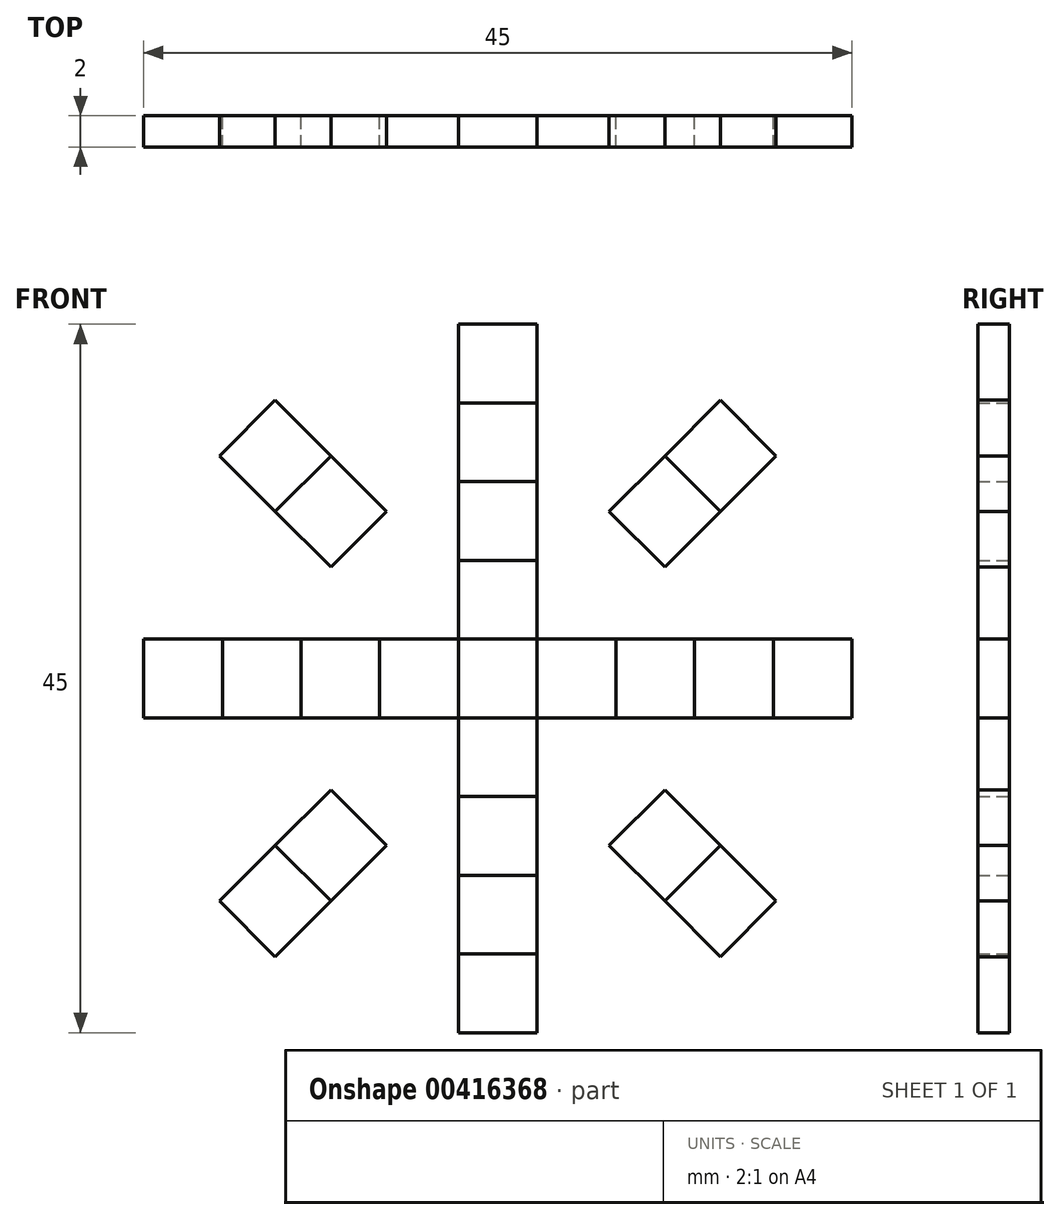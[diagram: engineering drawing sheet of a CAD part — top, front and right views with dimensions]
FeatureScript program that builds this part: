
annotation { "Feature Type Name" : "Feature", "Feature Type Description" : "" }
export const myFeature = defineFeature(function(context is Context, id is Id, definition is map)
    precondition{}
    {
        {
            var Q0;
            Q0=qCreatedBy(makeId("Front.planeOp"),FACE);
            var sketch = newSketch(context, id + "F0", { "sketchPlane" : qUnion([Q0])});
            skLineSegment(sketch, "E0", {"start": v(0, 0) * mm, "end": v(0, 2.5) * mm, "construction": true});
            skLineSegment(sketch, "E1", {"start": v(0, 2.5) * mm, "end": v(2.5, 2.5) * mm});
            skLineSegment(sketch, "E2", {"start": v(2.5, 2.5) * mm, "end": v(2.5, -2.5) * mm});
            skLineSegment(sketch, "E3", {"start": v(2.5, -2.5) * mm, "end": v(-2.5, -2.5) * mm});
            skLineSegment(sketch, "E4", {"start": v(-2.5, -2.5) * mm, "end": v(-2.5, 2.5) * mm});
            skLineSegment(sketch, "E5", {"start": v(-2.5, 2.5) * mm, "end": v(0, 2.5) * mm});
            skLineSegment(sketch, "E6", {"start": v(-2.5, 2.5) * mm, "end": v(-2.5, 7.5) * mm});
            skLineSegment(sketch, "E7", {"start": v(-2.5, 7.5) * mm, "end": v(2.5, 7.5) * mm});
            skLineSegment(sketch, "E8", {"start": v(2.5, 7.5) * mm, "end": v(2.5, 2.5) * mm});
            skLineSegment(sketch, "E9", {"start": v(2.5, 2.5) * mm, "end": v(7.5, 2.5) * mm});
            skLineSegment(sketch, "E10", {"start": v(7.5, 2.5) * mm, "end": v(7.5, -2.5) * mm});
            skLineSegment(sketch, "E11", {"start": v(7.5, -2.5) * mm, "end": v(2.5, -2.5) * mm});
            skLineSegment(sketch, "E12", {"start": v(2.5, -2.5) * mm, "end": v(2.5, -7.5) * mm});
            skLineSegment(sketch, "E13", {"start": v(2.5, -7.5) * mm, "end": v(-2.5, -7.5) * mm});
            skLineSegment(sketch, "E14", {"start": v(-2.5, -7.5) * mm, "end": v(-2.5, -2.5) * mm});
            skLineSegment(sketch, "E15", {"start": v(-2.5, -2.5) * mm, "end": v(-7.5, -2.5) * mm});
            skLineSegment(sketch, "E16", {"start": v(-7.5, -2.5) * mm, "end": v(-7.5, 2.5) * mm});
            skLineSegment(sketch, "E17", {"start": v(-7.5, 2.5) * mm, "end": v(-2.5, 2.5) * mm});
            skLineSegment(sketch, "E18", {"start": v(-7.5, -2.5) * mm, "end": v(-12.5, -2.5) * mm});
            skLineSegment(sketch, "E19", {"start": v(-12.5, -2.5) * mm, "end": v(-12.5, 2.5) * mm});
            skLineSegment(sketch, "E20", {"start": v(-12.5, 2.5) * mm, "end": v(-7.5, 2.5) * mm});
            skLineSegment(sketch, "E21", {"start": v(7.5, 2.5) * mm, "end": v(12.5, 2.5) * mm});
            skLineSegment(sketch, "E22", {"start": v(12.5, 2.5) * mm, "end": v(12.5, -2.5) * mm});
            skLineSegment(sketch, "E23", {"start": v(12.5, -2.5) * mm, "end": v(7.5, -2.5) * mm});
            skLineSegment(sketch, "E24", {"start": v(-2.5, 7.5) * mm, "end": v(-2.5, 12.5) * mm});
            skLineSegment(sketch, "E25", {"start": v(-2.5, 12.5) * mm, "end": v(2.5, 12.5) * mm});
            skLineSegment(sketch, "E26", {"start": v(2.5, 12.5) * mm, "end": v(2.5, 7.5) * mm});
            skLineSegment(sketch, "E27", {"start": v(2.5, -7.5) * mm, "end": v(2.5, -12.5) * mm});
            skLineSegment(sketch, "E28", {"start": v(2.5, -12.5) * mm, "end": v(-2.5, -12.5) * mm});
            skLineSegment(sketch, "E29", {"start": v(-2.5, -12.5) * mm, "end": v(-2.5, -7.5) * mm});
            skLineSegment(sketch, "E30", {"start": v(0, 2.5) * mm, "end": v(0, 12.5) * mm, "construction": true});
            skCircle(sketch, "E31.cCircle", {"center": v(0, 0) * mm, "radius": 12.5 * mm, "construction": true});
            skLineSegment(sketch, "E31.0", {"start": v(-5.18, 12.5) * mm, "end": v(5.18, 12.5) * mm, "construction": true});
            skLineSegment(sketch, "E31.1", {"start": v(5.18, 12.5) * mm, "end": v(12.5, 5.18) * mm, "construction": true});
            skLineSegment(sketch, "E31.2", {"start": v(12.5, 5.18) * mm, "end": v(12.5, -5.18) * mm, "construction": true});
            skLineSegment(sketch, "E31.3", {"start": v(12.5, -5.18) * mm, "end": v(5.18, -12.5) * mm, "construction": true});
            skLineSegment(sketch, "E31.4", {"start": v(5.18, -12.5) * mm, "end": v(-5.18, -12.5) * mm, "construction": true});
            skLineSegment(sketch, "E31.5", {"start": v(-5.18, -12.5) * mm, "end": v(-12.5, -5.18) * mm, "construction": true});
            skLineSegment(sketch, "E31.6", {"start": v(-12.5, -5.18) * mm, "end": v(-12.5, 5.18) * mm, "construction": true});
            skLineSegment(sketch, "E31.7", {"start": v(-12.5, 5.18) * mm, "end": v(-5.18, 12.5) * mm, "construction": true});
            skPoint(sketch, "E31.0.midPoint", {"position": v(0, 12.5) * mm});
            skLineSegment(sketch, "E32", {"start": v(8.84, 8.84) * mm, "end": v(10.6, 7.07) * mm});
            skLineSegment(sketch, "E33", {"start": v(10.6, 7.07) * mm, "end": v(14.14, 10.6) * mm});
            skLineSegment(sketch, "E34", {"start": v(14.14, 10.6) * mm, "end": v(10.6, 14.14) * mm});
            skLineSegment(sketch, "E35", {"start": v(8.84, 8.84) * mm, "end": v(7.07, 10.6) * mm});
            skLineSegment(sketch, "E36", {"start": v(8.84, -8.84) * mm, "end": v(7.07, -10.6) * mm});
            skLineSegment(sketch, "E37", {"start": v(7.07, -10.6) * mm, "end": v(10.6, -14.14) * mm});
            skLineSegment(sketch, "E38", {"start": v(10.6, -14.14) * mm, "end": v(14.14, -10.6) * mm});
            skLineSegment(sketch, "E39", {"start": v(14.14, -10.6) * mm, "end": v(10.6, -7.07) * mm});
            skLineSegment(sketch, "E40", {"start": v(10.6, -7.07) * mm, "end": v(8.84, -8.84) * mm});
            skLineSegment(sketch, "E41", {"start": v(-8.84, -8.84) * mm, "end": v(-10.6, -7.07) * mm});
            skLineSegment(sketch, "E42", {"start": v(-10.6, -7.07) * mm, "end": v(-14.14, -10.6) * mm});
            skLineSegment(sketch, "E43", {"start": v(-14.14, -10.6) * mm, "end": v(-10.6, -14.14) * mm});
            skLineSegment(sketch, "E44", {"start": v(-10.6, -14.14) * mm, "end": v(-7.07, -10.6) * mm});
            skLineSegment(sketch, "E45", {"start": v(-7.07, -10.6) * mm, "end": v(-8.84, -8.84) * mm});
            skLineSegment(sketch, "E46", {"start": v(10.6, 14.14) * mm, "end": v(7.07, 10.6) * mm});
            skLineSegment(sketch, "E47", {"start": v(12.5, 2.5) * mm, "end": v(22.5, 2.5) * mm});
            skLineSegment(sketch, "E48", {"start": v(22.5, 2.5) * mm, "end": v(22.5, -2.5) * mm});
            skLineSegment(sketch, "E49", {"start": v(22.5, -2.5) * mm, "end": v(12.5, -2.5) * mm});
            skLineSegment(sketch, "E50", {"start": v(2.5, -12.5) * mm, "end": v(2.5, -22.5) * mm});
            skLineSegment(sketch, "E51", {"start": v(2.5, -22.5) * mm, "end": v(-2.5, -22.5) * mm});
            skLineSegment(sketch, "E52", {"start": v(-2.5, -22.5) * mm, "end": v(-2.5, -12.5) * mm});
            skLineSegment(sketch, "E53", {"start": v(-12.5, -2.5) * mm, "end": v(-22.5, -2.5) * mm});
            skLineSegment(sketch, "E54", {"start": v(-22.5, -2.5) * mm, "end": v(-22.5, 2.5) * mm});
            skLineSegment(sketch, "E55", {"start": v(-22.5, 2.5) * mm, "end": v(-12.5, 2.5) * mm});
            skLineSegment(sketch, "E56", {"start": v(-2.5, 12.5) * mm, "end": v(-2.5, 22.5) * mm});
            skLineSegment(sketch, "E57", {"start": v(-2.5, 22.5) * mm, "end": v(2.5, 22.5) * mm});
            skLineSegment(sketch, "E58", {"start": v(2.5, 22.5) * mm, "end": v(2.5, 12.5) * mm});
            skLineSegment(sketch, "E59", {"start": v(17.5, 2.5) * mm, "end": v(17.5, -2.5) * mm});
            skLineSegment(sketch, "E60", {"start": v(2.5, -17.5) * mm, "end": v(-2.5, -17.5) * mm});
            skLineSegment(sketch, "E61", {"start": v(-17.5, -2.5) * mm, "end": v(-17.5, 2.5) * mm});
            skLineSegment(sketch, "E62", {"start": v(-2.5, 17.5) * mm, "end": v(2.5, 17.5) * mm});
            skLineSegment(sketch, "E63", {"start": v(10.6, -7.07) * mm, "end": v(-7.07, 10.6) * mm, "construction": true});
            skLineSegment(sketch, "E64", {"start": v(-7.07, 10.6) * mm, "end": v(-10.6, 14.14) * mm});
            skLineSegment(sketch, "E65", {"start": v(-10.6, 14.14) * mm, "end": v(-14.14, 10.6) * mm});
            skLineSegment(sketch, "E66", {"start": v(-14.14, 10.6) * mm, "end": v(-10.6, 7.07) * mm});
            skLineSegment(sketch, "E67", {"start": v(-10.6, 7.07) * mm, "end": v(-7.07, 10.6) * mm});
            skLineSegment(sketch, "E68", {"start": v(10.6, 14.14) * mm, "end": v(14.14, 17.68) * mm});
            skLineSegment(sketch, "E69", {"start": v(14.14, 17.68) * mm, "end": v(17.68, 14.14) * mm});
            skLineSegment(sketch, "E70", {"start": v(17.68, 14.14) * mm, "end": v(14.14, 10.6) * mm});
            skLineSegment(sketch, "E71", {"start": v(14.14, -10.6) * mm, "end": v(17.68, -14.14) * mm});
            skLineSegment(sketch, "E72", {"start": v(17.68, -14.14) * mm, "end": v(14.14, -17.68) * mm});
            skLineSegment(sketch, "E73", {"start": v(14.14, -17.68) * mm, "end": v(10.6, -14.14) * mm});
            skLineSegment(sketch, "E74", {"start": v(-10.6, -14.14) * mm, "end": v(-14.14, -17.68) * mm});
            skLineSegment(sketch, "E75", {"start": v(-14.14, -17.68) * mm, "end": v(-17.68, -14.14) * mm});
            skLineSegment(sketch, "E76", {"start": v(-17.68, -14.14) * mm, "end": v(-14.14, -10.6) * mm});
            skLineSegment(sketch, "E77", {"start": v(-14.14, 10.6) * mm, "end": v(-17.68, 14.14) * mm});
            skLineSegment(sketch, "E78", {"start": v(-17.68, 14.14) * mm, "end": v(-14.14, 17.68) * mm});
            skLineSegment(sketch, "E79", {"start": v(-14.14, 17.68) * mm, "end": v(-10.6, 14.14) * mm});
            skSolve(sketch);
        }
        {
            var Q0;
            Q0=makeQuery(id+"F0.imprint","IMPRINT",FACE,{"disambiguationData":[TD([[makeQuery(id+"F0.imprint","IMPRINT",EDGE,{"derivedFrom":sQuery(id+"F0.wireOp",EDGE,"E1")}),1.0]])]});
            var Q1;
            Q1=makeQuery(id+"F0.imprint","IMPRINT",FACE,{"disambiguationData":[TD([[makeQuery(id+"F0.imprint","IMPRINT",EDGE,{"derivedFrom":sQuery(id+"F0.wireOp",EDGE,"E2")}),1.0]])]});
            var Q2;
            Q2=makeQuery(id+"F0.imprint","IMPRINT",FACE,{"disambiguationData":[TD([[makeQuery(id+"F0.imprint","IMPRINT",EDGE,{"derivedFrom":sQuery(id+"F0.wireOp",EDGE,"E3")}),1.0]])]});
            var Q3;
            Q3=makeQuery(id+"F0.imprint","IMPRINT",FACE,{"disambiguationData":[TD([[makeQuery(id+"F0.imprint","IMPRINT",EDGE,{"derivedFrom":sQuery(id+"F0.wireOp",EDGE,"E4")}),1.0]])]});
            extrude(context, id + "F1", {"entities" : qUnion([Q0, Q1, Q2, Q3]), "depth" : 2 * mm});
        }
        {
            var Q0;
            Q0=makeQuery(id+"F0.imprint","IMPRINT",FACE,{"disambiguationData":[TD([[makeQuery(id+"F0.imprint","IMPRINT",EDGE,{"derivedFrom":sQuery(id+"F0.wireOp",EDGE,"E7")}),1.0]])]});
            var Q1;
            Q1=makeQuery(id+"F0.imprint","IMPRINT",FACE,{"disambiguationData":[TD([[makeQuery(id+"F0.imprint","IMPRINT",EDGE,{"derivedFrom":sQuery(id+"F0.wireOp",EDGE,"E10")}),1.0]])]});
            var Q2;
            Q2=makeQuery(id+"F0.imprint","IMPRINT",FACE,{"disambiguationData":[TD([[makeQuery(id+"F0.imprint","IMPRINT",EDGE,{"derivedFrom":sQuery(id+"F0.wireOp",EDGE,"E13")}),1.0]])]});
            var Q3;
            Q3=makeQuery(id+"F0.imprint","IMPRINT",FACE,{"disambiguationData":[TD([[makeQuery(id+"F0.imprint","IMPRINT",EDGE,{"derivedFrom":sQuery(id+"F0.wireOp",EDGE,"E16")}),1.0]])]});
            extrude(context, id + "F2", {"entities" : qUnion([Q0, Q1, Q2, Q3]), "depth" : 2 * mm});
        }
        {
            var Q0;
            {var subQ0=sQuery(id+"F0.wireOp",EDGE,"E25");Q0=makeQuery(id+"F0.imprint","IMPRINT",FACE,{"disambiguationData":[TD([[makeQuery(id+"F0.imprint","IMPRINT",EDGE,{"derivedFrom":subQ0}),1.0]])]});}
            var Q1;
            Q1=makeQuery(id+"F0.imprint","IMPRINT",FACE,{"disambiguationData":[TD([[makeQuery(id+"F0.imprint","IMPRINT",EDGE,{"derivedFrom":sQuery(id+"F0.wireOp",EDGE,"E32")}),1.0]])]});
            var Q2;
            {var subQ0=sQuery(id+"F0.wireOp",EDGE,"E22");Q2=makeQuery(id+"F0.imprint","IMPRINT",FACE,{"disambiguationData":[TD([[makeQuery(id+"F0.imprint","IMPRINT",EDGE,{"derivedFrom":subQ0}),1.0]])]});}
            var Q3;
            Q3=makeQuery(id+"F0.imprint","IMPRINT",FACE,{"disambiguationData":[TD([[makeQuery(id+"F0.imprint","IMPRINT",EDGE,{"derivedFrom":sQuery(id+"F0.wireOp",EDGE,"E36")}),1.0]])]});
            var Q4;
            {var subQ0=sQuery(id+"F0.wireOp",EDGE,"E28");Q4=makeQuery(id+"F0.imprint","IMPRINT",FACE,{"disambiguationData":[TD([[makeQuery(id+"F0.imprint","IMPRINT",EDGE,{"derivedFrom":subQ0}),1.0]])]});}
            var Q5;
            Q5=makeQuery(id+"F0.imprint","IMPRINT",FACE,{"disambiguationData":[TD([[makeQuery(id+"F0.imprint","IMPRINT",EDGE,{"derivedFrom":sQuery(id+"F0.wireOp",EDGE,"E41")}),1.0]])]});
            var Q6;
            {var subQ0=sQuery(id+"F0.wireOp",EDGE,"E19");Q6=makeQuery(id+"F0.imprint","IMPRINT",FACE,{"disambiguationData":[TD([[makeQuery(id+"F0.imprint","IMPRINT",EDGE,{"derivedFrom":subQ0}),1.0]])]});}
            var Q7;
            Q7=makeQuery(id+"F0.imprint","IMPRINT",FACE,{"disambiguationData":[TD([[makeQuery(id+"F0.imprint","IMPRINT",EDGE,{"derivedFrom":sQuery(id+"F0.wireOp",EDGE,"E64")}),1.0]])]});
            extrude(context, id + "F3", {"entities" : qUnion([Q0, Q1, Q2, Q3, Q4, Q5, Q6, Q7]), "depth" : 2 * mm});
        }
        {
            var Q0;
            {var subQ0=sQuery(id+"F0.wireOp",EDGE,"E57");Q0=makeQuery(id+"F0.imprint","IMPRINT",FACE,{"disambiguationData":[TD([[makeQuery(id+"F0.imprint","IMPRINT",EDGE,{"derivedFrom":subQ0}),-1.0]])]});}
            var Q1;
            Q1=makeQuery(id+"F0.imprint","IMPRINT",FACE,{"disambiguationData":[TD([[makeQuery(id+"F0.imprint","IMPRINT",EDGE,{"derivedFrom":sQuery(id+"F0.wireOp",EDGE,"E34")}),-1.0]])]});
            var Q2;
            {var subQ0=sQuery(id+"F0.wireOp",EDGE,"E48");Q2=makeQuery(id+"F0.imprint","IMPRINT",FACE,{"disambiguationData":[TD([[makeQuery(id+"F0.imprint","IMPRINT",EDGE,{"derivedFrom":subQ0}),-1.0]])]});}
            var Q3;
            Q3=makeQuery(id+"F0.imprint","IMPRINT",FACE,{"disambiguationData":[TD([[makeQuery(id+"F0.imprint","IMPRINT",EDGE,{"derivedFrom":sQuery(id+"F0.wireOp",EDGE,"E38")}),-1.0]])]});
            var Q4;
            {var subQ0=sQuery(id+"F0.wireOp",EDGE,"E51");Q4=makeQuery(id+"F0.imprint","IMPRINT",FACE,{"disambiguationData":[TD([[makeQuery(id+"F0.imprint","IMPRINT",EDGE,{"derivedFrom":subQ0}),-1.0]])]});}
            var Q5;
            Q5=makeQuery(id+"F0.imprint","IMPRINT",FACE,{"disambiguationData":[TD([[makeQuery(id+"F0.imprint","IMPRINT",EDGE,{"derivedFrom":sQuery(id+"F0.wireOp",EDGE,"E43")}),-1.0]])]});
            var Q6;
            {var subQ0=sQuery(id+"F0.wireOp",EDGE,"E54");Q6=makeQuery(id+"F0.imprint","IMPRINT",FACE,{"disambiguationData":[TD([[makeQuery(id+"F0.imprint","IMPRINT",EDGE,{"derivedFrom":subQ0}),-1.0]])]});}
            var Q7;
            Q7=makeQuery(id+"F0.imprint","IMPRINT",FACE,{"disambiguationData":[TD([[makeQuery(id+"F0.imprint","IMPRINT",EDGE,{"derivedFrom":sQuery(id+"F0.wireOp",EDGE,"E65")}),-1.0]])]});
            extrude(context, id + "F4", {"entities" : qUnion([Q0, Q1, Q2, Q3, Q4, Q5, Q6, Q7]), "depth" : 2 * mm});
        }
    });
